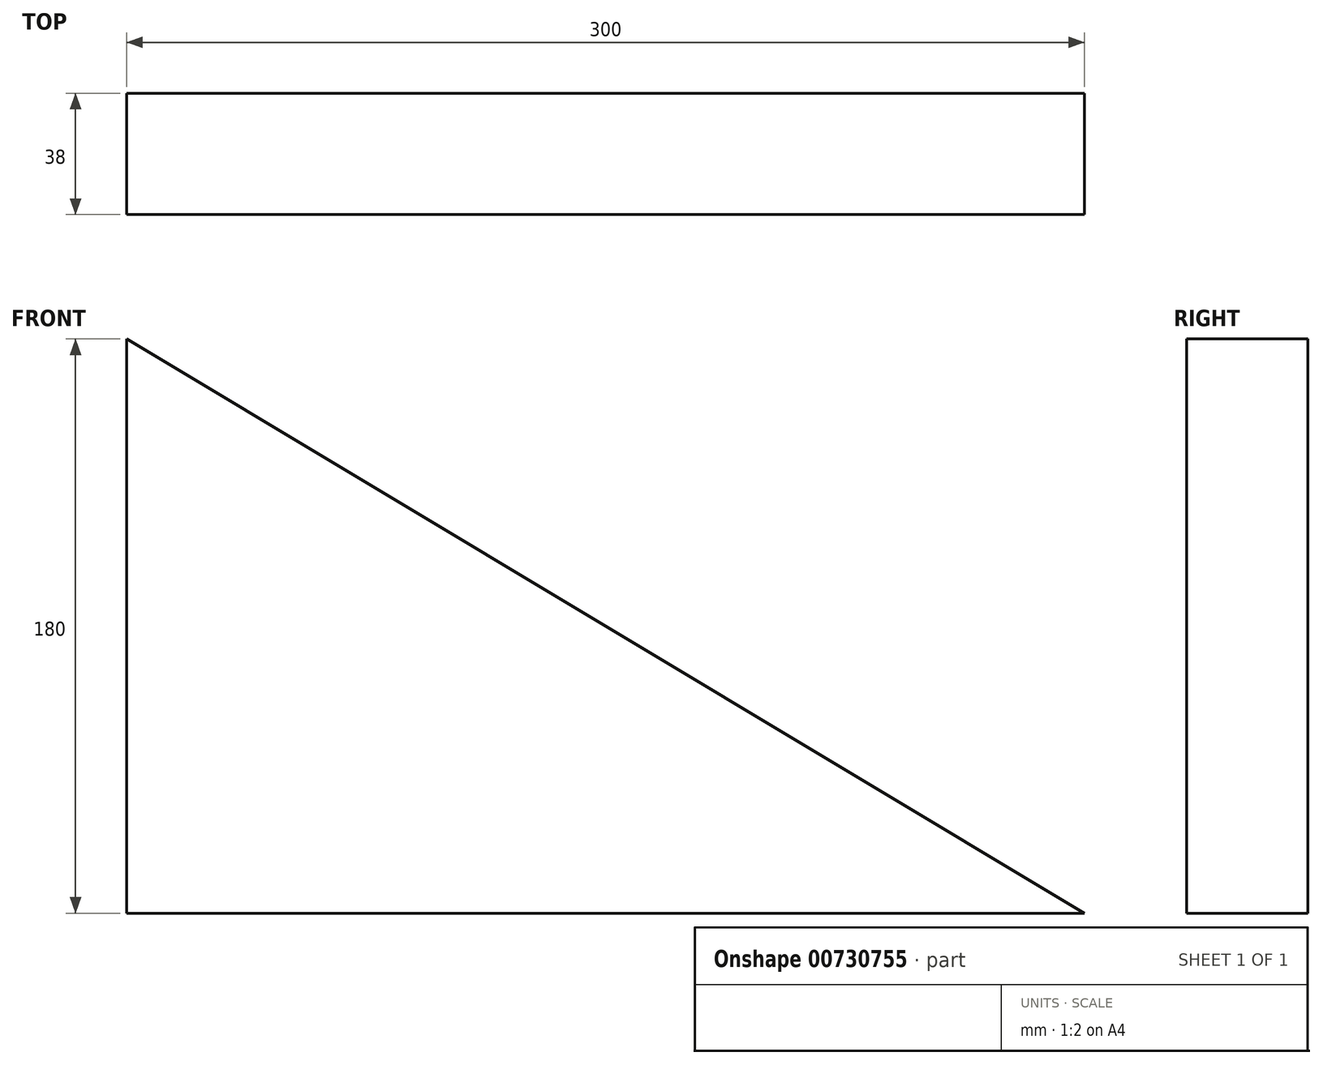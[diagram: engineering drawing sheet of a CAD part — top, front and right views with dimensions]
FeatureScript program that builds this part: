
annotation { "Feature Type Name" : "Feature", "Feature Type Description" : "" }
export const myFeature = defineFeature(function(context is Context, id is Id, definition is map)
    precondition{}
    {
        {
            var Q0;
            Q0=qCreatedBy(makeId("Front.planeOp"),FACE);
            var sketch = newSketch(context, id + "F0", { "sketchPlane" : qUnion([Q0])});
            skLineSegment(sketch, "E0", {"start": v(60.1, -62.48) * mm, "end": v(-239.9, -62.48) * mm});
            skLineSegment(sketch, "E1", {"start": v(-239.9, -62.48) * mm, "end": v(-239.9, 117.52) * mm});
            skLineSegment(sketch, "E2", {"start": v(-239.9, 117.52) * mm, "end": v(60.1, -62.48) * mm});
            skSolve(sketch);
        }
        {
            var Q0;
            Q0 = qSketchRegion(id + "F0", true);
            extrude(context, id + "F1", {"entities" : qUnion([Q0]), "endBound" : BoundingType.SYMMETRIC, "depth" : 38 * mm, "offsetDistance" : 25.4 * mm});
        }
    });
